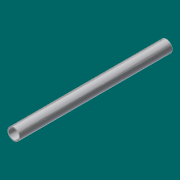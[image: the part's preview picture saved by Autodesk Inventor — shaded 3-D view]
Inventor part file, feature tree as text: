
AUTODESK INVENTOR PART (.ipt)
format: ipt  version: 2017 (Build 210142000, 142)  size: 112,128 bytes
history: native  units: in
note: dims shown in document units (in); Inventor stores cm internally (conversion verified against a paired STEP export)
features: extrude x1, sketch x1
ambient origin geometry x8: Origin, YZ Plane, XZ Plane, XY Plane, X Axis, Y Axis, Z Axis, Center Point
bodies: Solid1 (feature_tree)
feature tree (2):
  extrude  "Extrusion1"  Depth=36.25in
  sketch  "Sketch1"  dims[d0=2.875in d1=2.469in d2=36.25in d3=0.0in]
